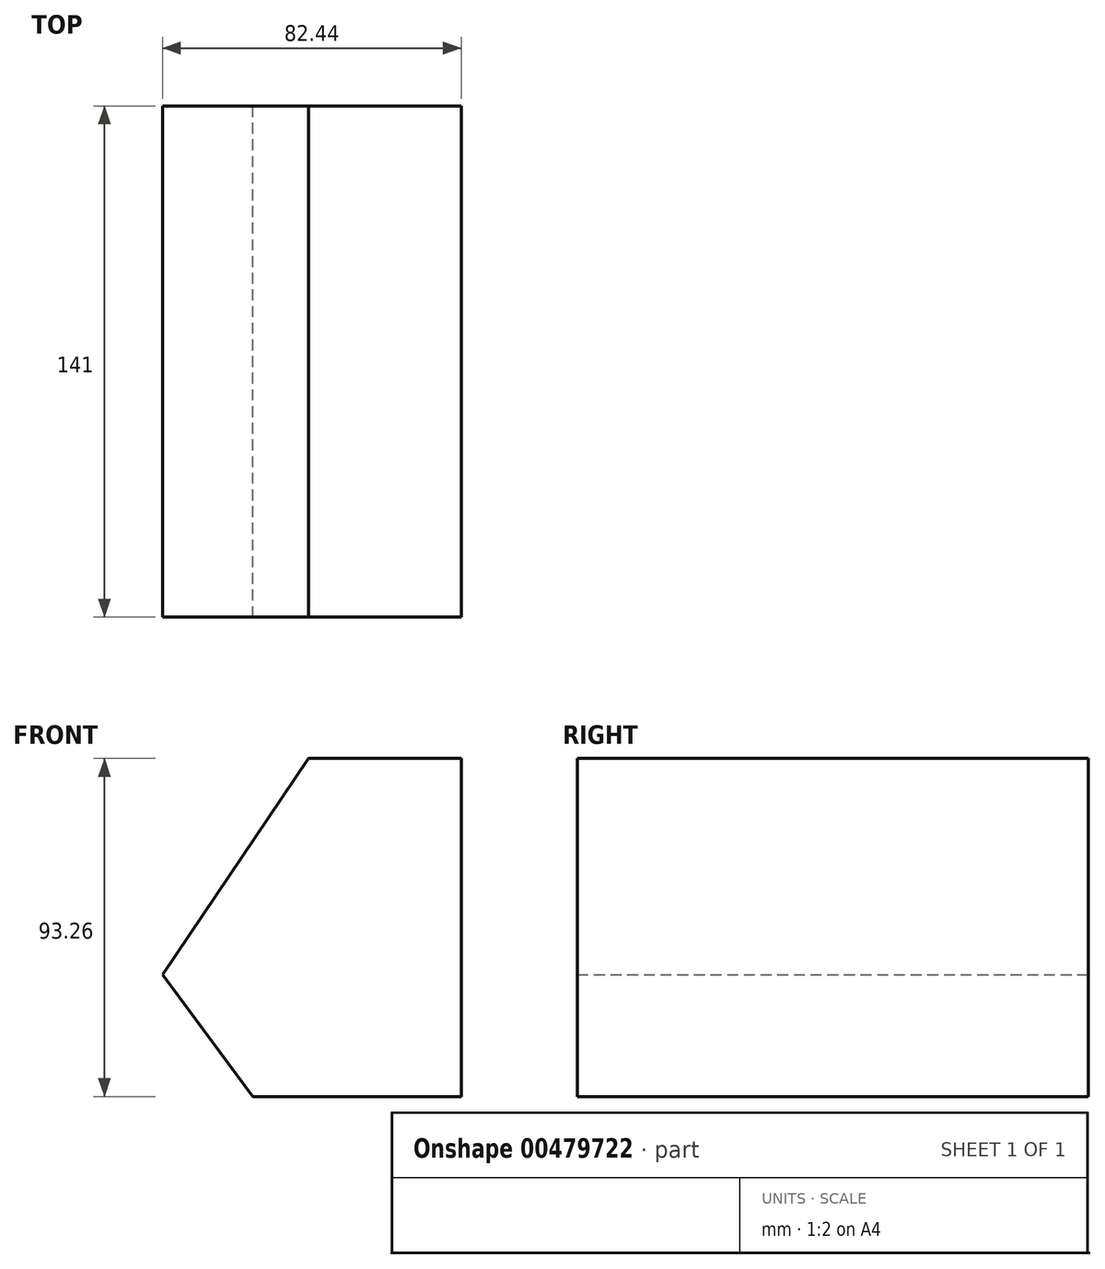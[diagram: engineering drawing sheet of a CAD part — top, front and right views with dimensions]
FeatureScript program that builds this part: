
annotation { "Feature Type Name" : "Feature", "Feature Type Description" : "" }
export const myFeature = defineFeature(function(context is Context, id is Id, definition is map)
    precondition{}
    {
        {
            var Q0;
            Q0=qCreatedBy(makeId("Front.planeOp"),FACE);
            var sketch = newSketch(context, id + "F0", { "sketchPlane" : qUnion([Q0])});
            skLineSegment(sketch, "E0", {"start": v(0, 0) * mm, "end": v(40.29, 59.69) * mm});
            skLineSegment(sketch, "E1", {"start": v(40.29, 59.69) * mm, "end": v(82.44, 59.69) * mm});
            skLineSegment(sketch, "E2", {"start": v(82.44, 59.69) * mm, "end": v(82.44, -33.57) * mm});
            skLineSegment(sketch, "E3", {"start": v(82.44, -33.57) * mm, "end": v(25, -33.57) * mm});
            skLineSegment(sketch, "E4", {"start": v(25, -33.57) * mm, "end": v(0, 0) * mm});
            skSolve(sketch);
        }
        {
            var Q0;
            Q0 = qSketchRegion(id + "F0", true);
            extrude(context, id + "F1", {"entities" : qUnion([Q0]), "depth" : 141 * mm});
        }
    });
